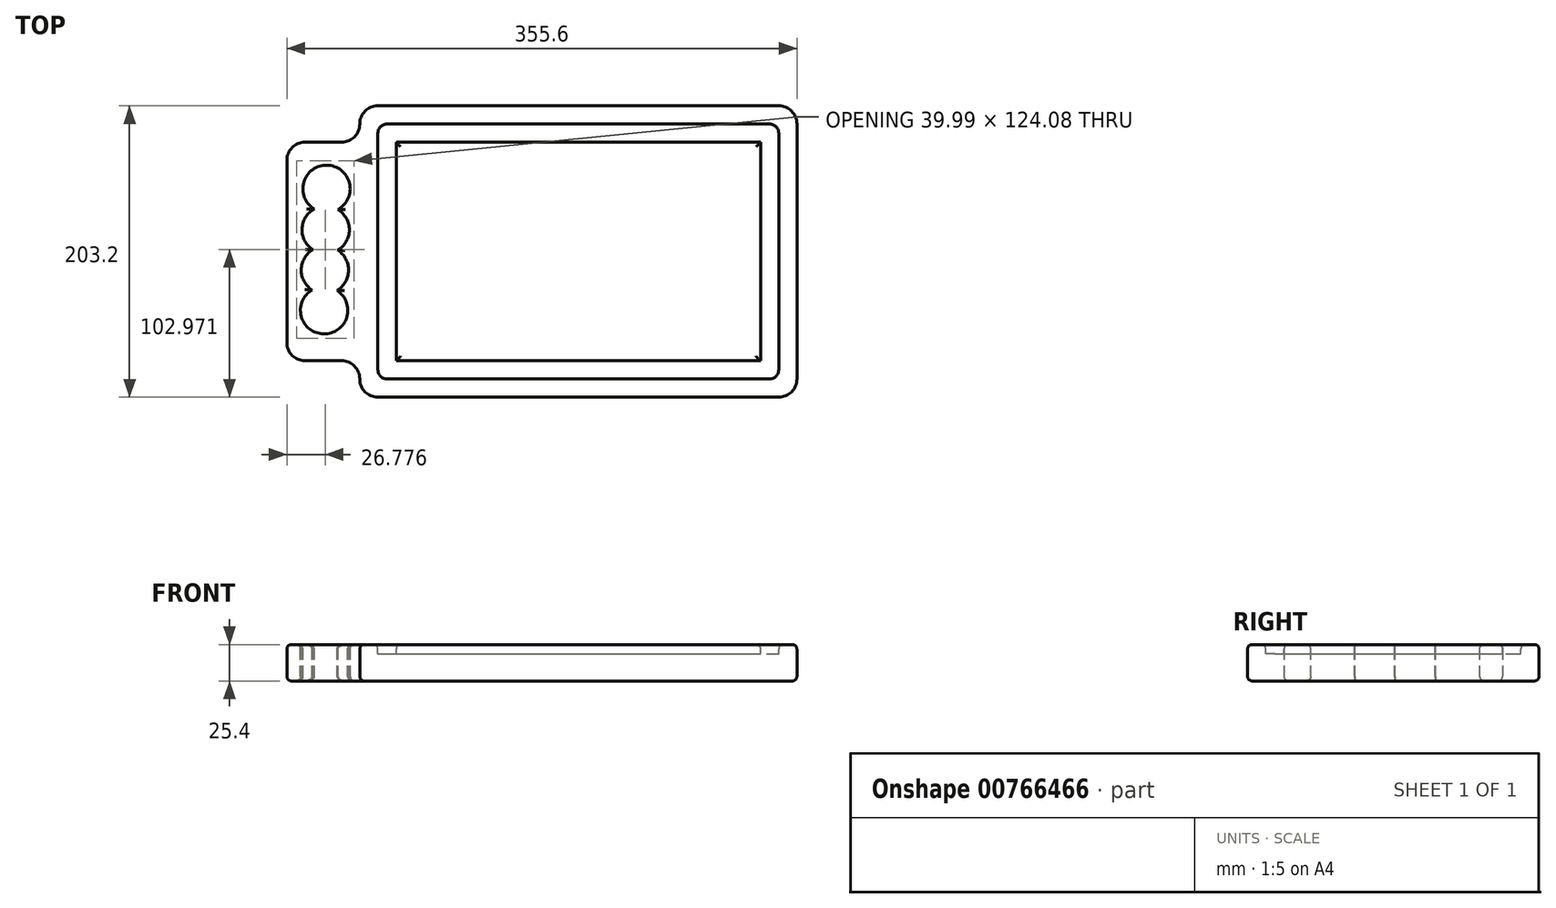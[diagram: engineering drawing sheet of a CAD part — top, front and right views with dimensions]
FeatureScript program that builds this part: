
annotation { "Feature Type Name" : "Feature", "Feature Type Description" : "" }
export const myFeature = defineFeature(function(context is Context, id is Id, definition is map)
    precondition{}
    {
        {
            var Q0;
            Q0=qCreatedBy(makeId("Top.planeOp"),FACE);
            var sketch = newSketch(context, id + "F0", { "sketchPlane" : qUnion([Q0])});
            skLineSegment(sketch, "E0.bottom", {"start": v(0, 0) * mm, "end": v(304.8, 0) * mm});
            skLineSegment(sketch, "E0.top", {"start": v(0, 203.2) * mm, "end": v(304.8, 203.2) * mm});
            skLineSegment(sketch, "E0.left", {"start": v(0, 0) * mm, "end": v(0, 203.2) * mm});
            skLineSegment(sketch, "E0.right", {"start": v(304.8, 0) * mm, "end": v(304.8, 203.2) * mm});
            skLineSegment(sketch, "E1.bottom", {"start": v(0, 177.8) * mm, "end": v(-50.8, 177.8) * mm});
            skLineSegment(sketch, "E1.top", {"start": v(0, 25.4) * mm, "end": v(-50.8, 25.4) * mm});
            skLineSegment(sketch, "E1.left", {"start": v(0, 177.8) * mm, "end": v(0, 25.4) * mm});
            skLineSegment(sketch, "E1.right", {"start": v(-50.8, 177.8) * mm, "end": v(-50.8, 25.4) * mm});
            skSolve(sketch);
        }
        {
            var Q0;
            Q0 = qSketchRegion(id + "F0", true);
            var Q1;
            {var subQ3=sQuery(id+"F0.wireOp",EDGE,"E0.bottom");Q1=makeQuery(id+"F0.imprint","IMPRINT",FACE,{"disambiguationData":[TD([[makeQuery(id+"F0.imprint","IMPRINT",EDGE,{"derivedFrom":subQ3}),1.0]])]});}
            extrude(context, id + "F1", {"entities" : qUnion([Q0, Q1]), "depth" : 25.4 * mm, "offsetDistance" : 25.4 * mm});
        }
        {
            var Q0;
            Q0=makeQuery(id+"F1.opExtrude","CAP_FACE",FACE,{"disambiguationData":[OSD([sQuery(id+"F0.wireOp",EDGE,"E0.bottom"),sQuery(id+"F0.wireOp",EDGE,"E0.top"),sQuery(id+"F0.wireOp",EDGE,"E0.left"),sQuery(id+"F0.wireOp",EDGE,"E0.right"),sQuery(id+"F0.wireOp",EDGE,"E1.bottom"),sQuery(id+"F0.wireOp",EDGE,"E1.top"),sQuery(id+"F0.wireOp",EDGE,"E1.right")])],"isStart":false});
            var sketch = newSketch(context, id + "F2", { "sketchPlane" : qUnion([Q0])});
            skArc(sketch, "E2", {"start": v(-15.2, 130.87) * mm, "mid": v(-22.85, 161.84) * mm, "end": v(-31.68, 131.18) * mm});
            skArc(sketch, "E3", {"start": v(-31.68, 131.18) * mm, "mid": v(-40.22, 117.31) * mm, "end": v(-32.7, 102.87) * mm});
            skArc(sketch, "E4", {"start": v(-32.7, 102.87) * mm, "mid": v(-40.77, 89) * mm, "end": v(-33.24, 74.81) * mm});
            skArc(sketch, "E5", {"start": v(-33.24, 74.81) * mm, "mid": v(-25.14, 44.1) * mm, "end": v(-15.84, 74.47) * mm});
            skArc(sketch, "E6.trimOffspring", {"start": v(-15.3, 102.53) * mm, "mid": v(-7.2, 116.67) * mm, "end": v(-15.2, 130.87) * mm});
            skArc(sketch, "E7.trimOffspring", {"start": v(-15.84, 74.47) * mm, "mid": v(-7.76, 88.34) * mm, "end": v(-15.3, 102.53) * mm});
            skSolve(sketch);
        }
        {
            var Q0;
            {var subQ4=sQuery(id+"F0.wireOp",EDGE,"E0.bottom");Q0=makeQuery(id+"F2.imprint","IMPRINT",FACE,{"disambiguationData":[TD([[makeQuery(id+"F2.imprint","IMPRINT",EDGE,{"derivedFrom":makeQuery(id+"F1.opExtrude","CAP_EDGE",EDGE,{"disambiguationData":[OSD([subQ4])],"isStart":false})}),1.0]])]});}
            var sketch = newSketch(context, id + "F3", { "sketchPlane" : qUnion([Q0])});
            skSolve(sketch);
        }
        {
            var Q0;
            Q0 = qSketchRegion(id + "F2", true);
            var Q1;
            Q1=makeQuery(id+"F3.imprint","IMPRINT",FACE,{"disambiguationData":[TD([[makeQuery(id+"F3.imprint","IMPRINT",EDGE,{"derivedFrom":makeQuery(id+"F2.imprint","IMPRINT",EDGE,{"derivedFrom":sQuery(id+"F2.wireOp",EDGE,"E2")})}),1.0]])]});
            extrude(context, id + "F4", {"entities" : qUnion([Q0, Q1]), "operationType" : NewBodyOperationType.REMOVE, "oppositeDirection" : true, "depth" : 25.4 * mm, "offsetDistance" : 25.4 * mm});
        }
        {
            var Q0;
            Q0=makeQuery(id+"F1.opExtrude","CAP_FACE",FACE,{"disambiguationData":[OSD([sQuery(id+"F0.wireOp",EDGE,"E0.bottom"),sQuery(id+"F0.wireOp",EDGE,"E0.top"),sQuery(id+"F0.wireOp",EDGE,"E0.left"),sQuery(id+"F0.wireOp",EDGE,"E0.right"),sQuery(id+"F0.wireOp",EDGE,"E1.bottom"),sQuery(id+"F0.wireOp",EDGE,"E1.top"),sQuery(id+"F0.wireOp",EDGE,"E1.right")])],"isStart":false});
            var sketch = newSketch(context, id + "F5", { "sketchPlane" : qUnion([Q0])});
            skLineSegment(sketch, "E8.0", {"start": v(12.7, 12.7) * mm, "end": v(12.7, 25.4) * mm});
            skLineSegment(sketch, "E8.1", {"start": v(12.7, 177.8) * mm, "end": v(12.7, 190.5) * mm});
            skLineSegment(sketch, "E8.2", {"start": v(12.7, 190.5) * mm, "end": v(292.1, 190.5) * mm});
            skLineSegment(sketch, "E8.3", {"start": v(292.1, 12.7) * mm, "end": v(292.1, 190.5) * mm});
            skLineSegment(sketch, "E8.4", {"start": v(12.7, 12.7) * mm, "end": v(292.1, 12.7) * mm});
            skLineSegment(sketch, "E9", {"start": v(12.7, 177.8) * mm, "end": v(12.7, 25.4) * mm});
            skLineSegment(sketch, "E10.0", {"start": v(25.4, 177.8) * mm, "end": v(25.4, 177.8) * mm});
            skLineSegment(sketch, "E10.1", {"start": v(279.4, 25.4) * mm, "end": v(279.4, 177.8) * mm});
            skLineSegment(sketch, "E10.2", {"start": v(25.4, 25.4) * mm, "end": v(279.4, 25.4) * mm});
            skLineSegment(sketch, "E10.3", {"start": v(25.4, 177.8) * mm, "end": v(279.4, 177.8) * mm});
            skLineSegment(sketch, "E10.4", {"start": v(25.4, 25.4) * mm, "end": v(25.4, 25.4) * mm});
            skLineSegment(sketch, "E10.5", {"start": v(25.4, 177.8) * mm, "end": v(25.4, 25.4) * mm});
            skSolve(sketch);
        }
        {
            var Q0;
            Q0=makeQuery(id+"F5.imprint","IMPRINT",FACE,{"disambiguationData":[TD([[makeQuery(id+"F5.imprint","IMPRINT",EDGE,{"derivedFrom":sQuery(id+"F5.wireOp",EDGE,"E8.0")}),-1.0]])]});
            extrude(context, id + "F6", {"entities" : qUnion([Q0]), "operationType" : NewBodyOperationType.REMOVE, "oppositeDirection" : true, "depth" : 6.35 * mm, "offsetDistance" : 25.4 * mm});
        }
        {
            var Q0;
            Q0=makeQuery(id+"F6.boolean.opBoolean","COPY",EDGE,{"derivedFrom":makeQuery(id+"F6.opExtrude","SWEPT_EDGE",EDGE,{"disambiguationData":[OSD([sQuery(id+"F5.wireOp",EDGE,"E8.1"),sQuery(id+"F5.wireOp",EDGE,"E8.2")])]})});
            var Q1;
            Q1=makeQuery(id+"F6.boolean.opBoolean","COPY",EDGE,{"derivedFrom":makeQuery(id+"F6.opExtrude","SWEPT_EDGE",EDGE,{"disambiguationData":[OSD([sQuery(id+"F5.wireOp",EDGE,"E8.2"),sQuery(id+"F5.wireOp",EDGE,"E8.3")])]})});
            var Q2;
            Q2=makeQuery(id+"F6.boolean.opBoolean","COPY",EDGE,{"derivedFrom":makeQuery(id+"F6.opExtrude","SWEPT_EDGE",EDGE,{"disambiguationData":[OSD([sQuery(id+"F5.wireOp",EDGE,"E8.3"),sQuery(id+"F5.wireOp",EDGE,"E8.4")])]})});
            var Q3;
            Q3=makeQuery(id+"F6.boolean.opBoolean","COPY",EDGE,{"derivedFrom":makeQuery(id+"F6.opExtrude","SWEPT_EDGE",EDGE,{"disambiguationData":[OSD([sQuery(id+"F5.wireOp",EDGE,"E8.0"),sQuery(id+"F5.wireOp",EDGE,"E8.4")])]})});
            fillet(context, id + "F7", {"entities" : qUnion([Q0, Q1, Q2, Q3]), "radius" : 6.35 * mm, "tangentPropagation" : true, "allowEdgeOverflow" : false});
        }
        {
            var Q0;
            Q0=makeQuery(id+"F1.opExtrude","SWEPT_EDGE",EDGE,{"disambiguationData":[OSD([sQuery(id+"F0.wireOp",EDGE,"E0.bottom"),sQuery(id+"F0.wireOp",EDGE,"E0.right")])]});
            var Q1;
            Q1=makeQuery(id+"F1.opExtrude","SWEPT_EDGE",EDGE,{"disambiguationData":[OSD([sQuery(id+"F0.wireOp",EDGE,"E0.top"),sQuery(id+"F0.wireOp",EDGE,"E0.right")])]});
            var Q2;
            Q2=makeQuery(id+"F1.opExtrude","SWEPT_EDGE",EDGE,{"disambiguationData":[OSD([sQuery(id+"F0.wireOp",EDGE,"E0.bottom"),sQuery(id+"F0.wireOp",EDGE,"E0.left")])]});
            var Q3;
            Q3=makeQuery(id+"F1.opExtrude","SWEPT_EDGE",EDGE,{"disambiguationData":[OSD([sQuery(id+"F0.wireOp",EDGE,"E1.top"),sQuery(id+"F0.wireOp",EDGE,"E1.right")])]});
            var Q4;
            Q4=makeQuery(id+"F1.opExtrude","SWEPT_EDGE",EDGE,{"disambiguationData":[OSD([sQuery(id+"F0.wireOp",EDGE,"E0.left"),sQuery(id+"F0.wireOp",EDGE,"E1.top"),sQuery(id+"F0.wireOp",EDGE,"E1.left")])]});
            var Q5;
            Q5=makeQuery(id+"F1.opExtrude","SWEPT_EDGE",EDGE,{"disambiguationData":[OSD([sQuery(id+"F0.wireOp",EDGE,"E1.bottom"),sQuery(id+"F0.wireOp",EDGE,"E1.right")])]});
            var Q6;
            Q6=makeQuery(id+"F1.opExtrude","SWEPT_EDGE",EDGE,{"disambiguationData":[OSD([sQuery(id+"F0.wireOp",EDGE,"E0.left"),sQuery(id+"F0.wireOp",EDGE,"E1.bottom"),sQuery(id+"F0.wireOp",EDGE,"E1.left")])]});
            var Q7;
            Q7=makeQuery(id+"F1.opExtrude","SWEPT_EDGE",EDGE,{"disambiguationData":[OSD([sQuery(id+"F0.wireOp",EDGE,"E0.top"),sQuery(id+"F0.wireOp",EDGE,"E0.left")])]});
            fillet(context, id + "F8", {"entities" : qUnion([Q0, Q1, Q2, Q3, Q4, Q5, Q6, Q7]), "radius" : 12.7 * mm, "tangentPropagation" : true, "allowEdgeOverflow" : false});
        }
        {
            var Q0;
            Q0=makeQuery(id+"F6.boolean.opBoolean","SPLIT",FACE,{"disambiguationData":[TD([makeQuery(id+"F6.opExtrude","SWEPT_FACE",FACE,{"disambiguationData":[OSD([sQuery(id+"F5.wireOp",EDGE,"E10.1")])]})])],"derivedFrom":makeQuery(id+"F1.opExtrude","CAP_FACE",FACE,{"disambiguationData":[OSD([sQuery(id+"F0.wireOp",EDGE,"E0.bottom"),sQuery(id+"F0.wireOp",EDGE,"E0.top"),sQuery(id+"F0.wireOp",EDGE,"E0.left"),sQuery(id+"F0.wireOp",EDGE,"E0.right"),sQuery(id+"F0.wireOp",EDGE,"E1.bottom"),sQuery(id+"F0.wireOp",EDGE,"E1.top"),sQuery(id+"F0.wireOp",EDGE,"E1.right")])],"isStart":false})});
            var Q1;
            {var subQ1=sQuery(id+"F0.wireOp",EDGE,"E1.top");var subQ2=sQuery(id+"F0.wireOp",EDGE,"E1.right");var subQ4=sQuery(id+"F0.wireOp",EDGE,"E1.bottom");var subQ5=sQuery(id+"F0.wireOp",EDGE,"E0.right");var subQ6=sQuery(id+"F0.wireOp",EDGE,"E0.bottom");var subQ7=sQuery(id+"F0.wireOp",EDGE,"E0.left");var subQ8=sQuery(id+"F0.wireOp",EDGE,"E0.top");Q1=makeQuery(id+"F6.boolean.opBoolean","SPLIT",FACE,{"disambiguationData":[TD([makeQuery(id+"F1.opExtrude","SWEPT_FACE",FACE,{"disambiguationData":[OSD([subQ6])]})])],"derivedFrom":makeQuery(id+"F1.opExtrude","CAP_FACE",FACE,{"disambiguationData":[OSD([subQ6,subQ8,subQ7,subQ5,subQ4,subQ1,subQ2])],"isStart":false})});}
            var Q2;
            Q2=makeQuery(id+"F1.opExtrude","CAP_FACE",FACE,{"disambiguationData":[OSD([sQuery(id+"F0.wireOp",EDGE,"E0.bottom"),sQuery(id+"F0.wireOp",EDGE,"E0.top"),sQuery(id+"F0.wireOp",EDGE,"E0.left"),sQuery(id+"F0.wireOp",EDGE,"E0.right"),sQuery(id+"F0.wireOp",EDGE,"E1.bottom"),sQuery(id+"F0.wireOp",EDGE,"E1.top"),sQuery(id+"F0.wireOp",EDGE,"E1.right")])],"isStart":true});
            fillet(context, id + "F9", {"entities" : qUnion([Q0, Q1, Q2]), "radius" : 3.17 * mm, "tangentPropagation" : true, "allowEdgeOverflow" : false});
        }
    });
